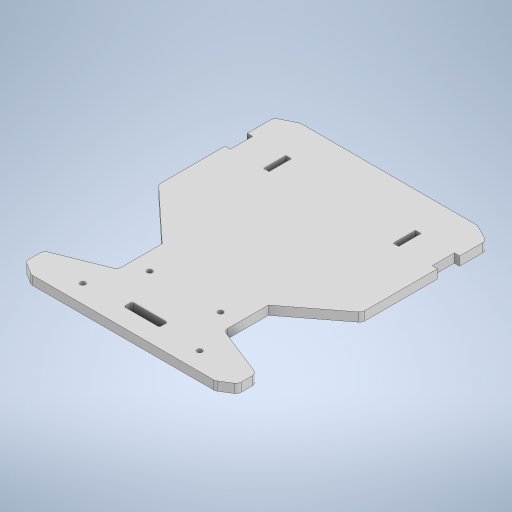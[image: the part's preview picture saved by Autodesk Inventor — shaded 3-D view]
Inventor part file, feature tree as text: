
AUTODESK INVENTOR PART (.ipt)
format: ipt  version: 2023 (Build 270158000, 158)  size: 343,552 bytes
history: native  units: in
note: dims shown in document units (in); Inventor stores cm internally (conversion verified against a paired STEP export)
features: fillet x2, extrude x1, sketch x1
ambient origin geometry x8: Origin, YZ Plane, XZ Plane, XY Plane, X Axis, Y Axis, Z Axis, Center Point
bodies: Solid1 (feature_tree)
feature tree (4):
  extrude  "Extrusion1"  Depth=5.9055in
  fillet  "Fillet1"  Radius=0.7874in
  fillet  "Fillet2"  Radius=0.1181in
  sketch  "Sketch1"  dims[d0=4.7244in d1=5.9055in d2=0.7874in d3=0.1181in d4=0.1181in d5=0.4921in d6=0.7441in d7=0.1181in d8=0.4016in d9=1.2992in d10=2.5984in d11=0.1102in d12=0.1102in d13=1.378in d14=0.7874in d15=1.5748in d16=0.1102in d17=0.1102in d18=2.7559in d19=0.5906in d20=0.3937in d21=0.3937in d22=1.1811in d23=1.1811in d24=0.315in d25=0.315in d26=0.7874in d27=0.1181in d28=0.4921in d29=0.7441in d30=0.1181in d31=0.315in d32=0.1969in d33=0.315in d34=0.1969in d35=0.3937in d36=0.1969in d37=0.3937in d38=0.1969in d39=0.1969in d40=0.0in d41=0.1181in d42=0.0787in d43=0.3937in d44=0.7874in d45=0.1378in d46=0.0394in d47=0.9843in d48=0.9843in]
